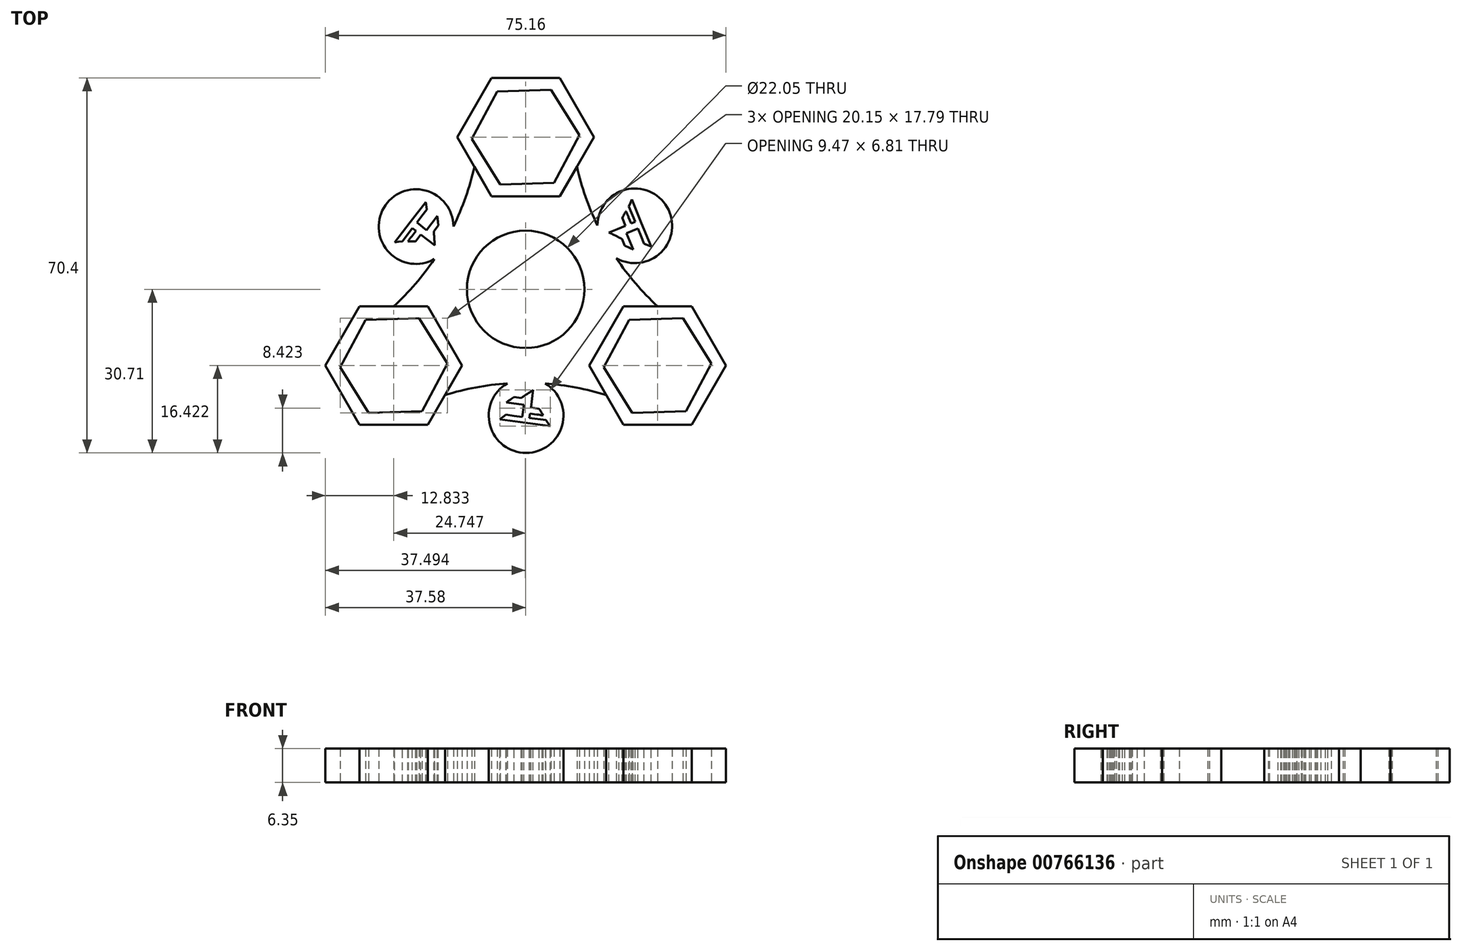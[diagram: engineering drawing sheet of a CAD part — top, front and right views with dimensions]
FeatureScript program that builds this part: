
annotation { "Feature Type Name" : "Feature", "Feature Type Description" : "" }
export const myFeature = defineFeature(function(context is Context, id is Id, definition is map)
    precondition{}
    {
        {
            var Q0;
            Q0=qCreatedBy(makeId("Top.planeOp"),FACE);
            var sketch = newSketch(context, id + "F0", { "sketchPlane" : qUnion([Q0])});
            skCircle(sketch, "E0.cCircle", {"center": v(0, 28.57) * mm, "radius": 8.73 * mm, "construction": true});
            skLineSegment(sketch, "E0.0", {"start": v(-4.75, 19.68) * mm, "end": v(-10.08, 28.24) * mm});
            skLineSegment(sketch, "E0.1", {"start": v(-10.08, 28.24) * mm, "end": v(-5.33, 37.14) * mm});
            skLineSegment(sketch, "E0.2", {"start": v(-5.33, 37.14) * mm, "end": v(4.75, 37.47) * mm});
            skLineSegment(sketch, "E0.3", {"start": v(4.75, 37.47) * mm, "end": v(10.08, 28.9) * mm});
            skLineSegment(sketch, "E0.4", {"start": v(10.08, 28.9) * mm, "end": v(5.33, 20.01) * mm});
            skLineSegment(sketch, "E0.5", {"start": v(5.33, 20.01) * mm, "end": v(-4.75, 19.68) * mm});
            skPoint(sketch, "E0.0.midPoint", {"position": v(-7.41, 23.96) * mm});
            skCircle(sketch, "E1.cCircle", {"center": v(0, 28.57) * mm, "radius": 11.11 * mm, "construction": true});
            skLineSegment(sketch, "E1.0", {"start": v(6.42, 17.46) * mm, "end": v(-6.42, 17.46) * mm});
            skLineSegment(sketch, "E1.1", {"start": v(-6.42, 17.46) * mm, "end": v(-12.83, 28.57) * mm});
            skLineSegment(sketch, "E1.2", {"start": v(-12.83, 28.57) * mm, "end": v(-6.42, 39.69) * mm});
            skLineSegment(sketch, "E1.3", {"start": v(-6.42, 39.69) * mm, "end": v(6.42, 39.69) * mm});
            skLineSegment(sketch, "E1.4", {"start": v(6.42, 39.69) * mm, "end": v(12.83, 28.57) * mm});
            skLineSegment(sketch, "E1.5", {"start": v(12.83, 28.57) * mm, "end": v(6.42, 17.46) * mm});
            skPoint(sketch, "E1.0.midPoint", {"position": v(0, 17.46) * mm});
            skLineSegment(sketch, "E2.1.0", {"start": v(-30.07, -5.73) * mm, "end": v(-20, -5.4) * mm});
            skPoint(sketch, "E2.1.1", {"position": v(-17.05, -18.4) * mm});
            skPoint(sketch, "E2.1.2", {"position": v(-15.12, -8.73) * mm});
            skLineSegment(sketch, "E2.1.3", {"start": v(-31.16, -3.17) * mm, "end": v(-18.33, -3.17) * mm});
            skLineSegment(sketch, "E2.1.4", {"start": v(-11.92, -14.29) * mm, "end": v(-18.33, -25.4) * mm});
            skLineSegment(sketch, "E2.1.5", {"start": v(-18.33, -3.17) * mm, "end": v(-11.92, -14.29) * mm});
            skLineSegment(sketch, "E2.1.6", {"start": v(-20, -5.4) * mm, "end": v(-14.67, -13.95) * mm});
            skLineSegment(sketch, "E2.1.7", {"start": v(-14.67, -13.95) * mm, "end": v(-19.42, -22.85) * mm});
            skLineSegment(sketch, "E2.1.8", {"start": v(-18.33, -25.4) * mm, "end": v(-31.16, -25.4) * mm});
            skCircle(sketch, "E2.1.9", {"center": v(-24.75, -14.29) * mm, "radius": 11.11 * mm, "construction": true});
            skLineSegment(sketch, "E2.1.10", {"start": v(-31.16, -25.4) * mm, "end": v(-37.58, -14.29) * mm});
            skCircle(sketch, "E2.1.11", {"center": v(-24.75, -14.29) * mm, "radius": 8.73 * mm, "construction": true});
            skLineSegment(sketch, "E2.1.12", {"start": v(-19.42, -22.85) * mm, "end": v(-29.5, -23.18) * mm});
            skLineSegment(sketch, "E2.1.13", {"start": v(-34.82, -14.62) * mm, "end": v(-30.07, -5.73) * mm});
            skLineSegment(sketch, "E2.1.14", {"start": v(-37.58, -14.29) * mm, "end": v(-31.16, -3.17) * mm});
            skLineSegment(sketch, "E2.1.15", {"start": v(-29.5, -23.18) * mm, "end": v(-34.82, -14.62) * mm});
            skLineSegment(sketch, "E2.2.0", {"start": v(20, -23.18) * mm, "end": v(14.67, -14.62) * mm});
            skPoint(sketch, "E2.2.1", {"position": v(24.46, -5.56) * mm});
            skPoint(sketch, "E2.2.2", {"position": v(15.12, -8.73) * mm});
            skLineSegment(sketch, "E2.2.3", {"start": v(18.33, -25.4) * mm, "end": v(11.92, -14.29) * mm});
            skLineSegment(sketch, "E2.2.4", {"start": v(18.33, -3.18) * mm, "end": v(31.16, -3.18) * mm});
            skLineSegment(sketch, "E2.2.5", {"start": v(11.92, -14.29) * mm, "end": v(18.33, -3.18) * mm});
            skLineSegment(sketch, "E2.2.6", {"start": v(14.67, -14.62) * mm, "end": v(19.42, -5.73) * mm});
            skLineSegment(sketch, "E2.2.7", {"start": v(19.42, -5.73) * mm, "end": v(29.5, -5.4) * mm});
            skLineSegment(sketch, "E2.2.8", {"start": v(31.16, -3.18) * mm, "end": v(37.58, -14.29) * mm});
            skCircle(sketch, "E2.2.9", {"center": v(24.75, -14.29) * mm, "radius": 11.11 * mm, "construction": true});
            skLineSegment(sketch, "E2.2.10", {"start": v(37.58, -14.29) * mm, "end": v(31.16, -25.4) * mm});
            skCircle(sketch, "E2.2.11", {"center": v(24.75, -14.29) * mm, "radius": 8.73 * mm, "construction": true});
            skLineSegment(sketch, "E2.2.12", {"start": v(29.5, -5.4) * mm, "end": v(34.82, -13.95) * mm});
            skLineSegment(sketch, "E2.2.13", {"start": v(30.07, -22.85) * mm, "end": v(20, -23.18) * mm});
            skLineSegment(sketch, "E2.2.14", {"start": v(31.16, -25.4) * mm, "end": v(18.33, -25.4) * mm});
            skLineSegment(sketch, "E2.2.15", {"start": v(34.82, -13.95) * mm, "end": v(30.07, -22.85) * mm});
            skPoint(sketch, "E2.center", {"position": v(0, 0) * mm});
            skSolve(sketch);
        }
        {
            var Q0;
            Q0=qCreatedBy(makeId("Top.planeOp"),FACE);
            var sketch = newSketch(context, id + "F1", { "sketchPlane" : qUnion([Q0])});
            skLineSegment(sketch, "E3.0", {"start": v(6.42, 39.69) * mm, "end": v(12.83, 28.57) * mm});
            skLineSegment(sketch, "E3.1", {"start": v(-29.5, -23.18) * mm, "end": v(-34.82, -14.62) * mm});
            skLineSegment(sketch, "E3.2", {"start": v(-34.82, -14.62) * mm, "end": v(-30.07, -5.73) * mm});
            skLineSegment(sketch, "E3.3", {"start": v(34.82, -13.95) * mm, "end": v(30.07, -22.85) * mm});
            skCircle(sketch, "E3.4", {"center": v(-24.75, -14.29) * mm, "radius": 8.73 * mm});
            skLineSegment(sketch, "E3.5", {"start": v(30.07, -22.85) * mm, "end": v(20, -23.18) * mm});
            skLineSegment(sketch, "E3.6", {"start": v(29.5, -5.4) * mm, "end": v(34.82, -13.95) * mm});
            skLineSegment(sketch, "E3.7", {"start": v(-31.16, -25.4) * mm, "end": v(-37.58, -14.29) * mm});
            skLineSegment(sketch, "E3.8", {"start": v(11.92, -14.29) * mm, "end": v(18.33, -3.18) * mm});
            skLineSegment(sketch, "E3.9", {"start": v(18.33, -25.4) * mm, "end": v(11.92, -14.29) * mm});
            skLineSegment(sketch, "E3.10", {"start": v(37.58, -14.29) * mm, "end": v(31.16, -25.4) * mm});
            skLineSegment(sketch, "E3.11", {"start": v(-18.33, -25.4) * mm, "end": v(-31.16, -25.4) * mm});
            skLineSegment(sketch, "E3.12", {"start": v(31.16, -3.18) * mm, "end": v(37.58, -14.29) * mm});
            skLineSegment(sketch, "E3.13", {"start": v(-20, -5.4) * mm, "end": v(-14.67, -13.95) * mm});
            skLineSegment(sketch, "E3.14", {"start": v(14.67, -14.62) * mm, "end": v(19.42, -5.73) * mm});
            skLineSegment(sketch, "E3.15", {"start": v(-11.92, -14.29) * mm, "end": v(-18.33, -25.4) * mm});
            skCircle(sketch, "E3.16", {"center": v(0, 0) * mm, "radius": 11.02 * mm});
            skCircle(sketch, "E3.17", {"center": v(0, 0) * mm, "radius": 14.29 * mm});
            skLineSegment(sketch, "E3.18", {"start": v(12.83, 28.57) * mm, "end": v(6.42, 17.46) * mm});
            skLineSegment(sketch, "E3.19", {"start": v(-30.07, -5.73) * mm, "end": v(-20, -5.4) * mm});
            skLineSegment(sketch, "E3.20", {"start": v(-31.16, -3.17) * mm, "end": v(-18.33, -3.17) * mm});
            skLineSegment(sketch, "E3.21", {"start": v(20, -23.18) * mm, "end": v(14.67, -14.62) * mm});
            skCircle(sketch, "E3.22", {"center": v(0, 28.57) * mm, "radius": 8.73 * mm});
            skLineSegment(sketch, "E3.23", {"start": v(-10.08, 28.24) * mm, "end": v(-5.33, 37.14) * mm});
            skLineSegment(sketch, "E3.24", {"start": v(-5.33, 37.14) * mm, "end": v(4.75, 37.47) * mm});
            skLineSegment(sketch, "E3.25", {"start": v(-19.42, -22.85) * mm, "end": v(-29.5, -23.18) * mm});
            skLineSegment(sketch, "E3.26", {"start": v(10.08, 28.9) * mm, "end": v(5.33, 20.01) * mm});
            skLineSegment(sketch, "E3.27", {"start": v(4.75, 37.47) * mm, "end": v(10.08, 28.9) * mm});
            skLineSegment(sketch, "E3.28", {"start": v(31.16, -25.4) * mm, "end": v(18.33, -25.4) * mm});
            skCircle(sketch, "E3.29", {"center": v(0, 28.57) * mm, "radius": 11.11 * mm});
            skCircle(sketch, "E3.30", {"center": v(24.75, -14.29) * mm, "radius": 8.73 * mm});
            skLineSegment(sketch, "E3.31", {"start": v(18.33, -3.18) * mm, "end": v(31.16, -3.18) * mm});
            skCircle(sketch, "E3.32", {"center": v(-24.75, -14.29) * mm, "radius": 11.11 * mm});
            skLineSegment(sketch, "E3.33", {"start": v(6.42, 17.46) * mm, "end": v(-6.42, 17.46) * mm});
            skLineSegment(sketch, "E3.34", {"start": v(-6.42, 17.46) * mm, "end": v(-12.83, 28.57) * mm});
            skLineSegment(sketch, "E3.35", {"start": v(-37.58, -14.29) * mm, "end": v(-31.16, -3.17) * mm});
            skCircle(sketch, "E3.36", {"center": v(24.75, -14.29) * mm, "radius": 11.11 * mm});
            skLineSegment(sketch, "E3.37", {"start": v(-12.83, 28.57) * mm, "end": v(-6.42, 39.69) * mm});
            skLineSegment(sketch, "E3.38", {"start": v(-6.42, 39.69) * mm, "end": v(6.42, 39.69) * mm});
            skLineSegment(sketch, "E3.39", {"start": v(-18.33, -3.17) * mm, "end": v(-11.92, -14.29) * mm});
            skPoint(sketch, "E4.endSnap0", {"position": v(-25.03, -5.56) * mm});
            skArc(sketch, "E5", {"start": v(9.62, 23.02) * mm, "mid": v(15.2, 8.77) * mm, "end": v(24.75, -3.18) * mm});
            skArc(sketch, "E6", {"start": v(-24.75, -3.18) * mm, "mid": v(-15.2, 8.77) * mm, "end": v(-9.62, 23.02) * mm});
            skArc(sketch, "E7", {"start": v(15.12, -19.84) * mm, "mid": v(0, -17.54) * mm, "end": v(-15.12, -19.84) * mm});
            skCircle(sketch, "E8", {"center": v(-20.57, 11.77) * mm, "radius": 7 * mm});
            skCircle(sketch, "E9.1.0", {"center": v(0.09, -23.7) * mm, "radius": 7 * mm});
            skCircle(sketch, "E9.2.0", {"center": v(20.48, 11.93) * mm, "radius": 7 * mm});
            skSolve(sketch);
        }
        {
            var Q0;
            {var subQ0=sQuery(id+"F1.wireOp",EDGE,"E8");var subQ1=sQuery(id+"F1.wireOp",EDGE,"E6");var subQ2=makeQuery(id+"F1.imprint","INTERSECT",VERTEX,{"disambiguationData":[OD(0.0)],"derivedFrom":[subQ1,subQ0]});Q0=makeQuery(id+"F1.imprint","IMPRINT",FACE,{"disambiguationData":[TD([[makeQuery(id+"F1.imprint","IMPRINT",EDGE,{"disambiguationData":[TD([[subQ2,-1.0]])],"derivedFrom":subQ1}),1.0]])]});}
            var Q1;
            {var subQ0=sQuery(id+"F1.wireOp",EDGE,"E9.2.0");var subQ1=sQuery(id+"F1.wireOp",EDGE,"E5");var subQ2=makeQuery(id+"F1.imprint","INTERSECT",VERTEX,{"disambiguationData":[OD(0.0)],"derivedFrom":[subQ1,subQ0]});Q1=makeQuery(id+"F1.imprint","IMPRINT",FACE,{"disambiguationData":[TD([[makeQuery(id+"F1.imprint","IMPRINT",EDGE,{"disambiguationData":[TD([[subQ2,-1.0]])],"derivedFrom":subQ1}),1.0]])]});}
            var Q2;
            Q2=makeQuery(id+"F0.imprint","IMPRINT",FACE,{"disambiguationData":[TD([[makeQuery(id+"F0.imprint","IMPRINT",EDGE,{"derivedFrom":sQuery(id+"F0.wireOp",EDGE,"E2.2.0")}),1.0]])]});
            var Q3;
            Q3=makeQuery(id+"F0.imprint","IMPRINT",FACE,{"disambiguationData":[TD([[makeQuery(id+"F0.imprint","IMPRINT",EDGE,{"derivedFrom":sQuery(id+"F0.wireOp",EDGE,"E2.1.0")}),1.0]])]});
            var Q4;
            {var subQ0=sQuery(id+"F1.wireOp",EDGE,"E9.1.0");var subQ1=sQuery(id+"F1.wireOp",EDGE,"E7");var subQ2=makeQuery(id+"F1.imprint","INTERSECT",VERTEX,{"disambiguationData":[OD(0.0)],"derivedFrom":[subQ1,subQ0]});Q4=makeQuery(id+"F1.imprint","IMPRINT",FACE,{"disambiguationData":[TD([[makeQuery(id+"F1.imprint","IMPRINT",EDGE,{"disambiguationData":[TD([[subQ2,-1.0]])],"derivedFrom":subQ1}),1.0]])]});}
            var Q5;
            Q5=makeQuery(id+"F1.imprint","IMPRINT",FACE,{"disambiguationData":[TD([[makeQuery(id+"F1.imprint","IMPRINT",EDGE,{"derivedFrom":sQuery(id+"F1.wireOp",EDGE,"E3.17")}),-1.0]])]});
            var Q6;
            {var subQ0=sQuery(id+"F1.wireOp",EDGE,"E9.2.0");var subQ1=sQuery(id+"F1.wireOp",EDGE,"E5");var subQ2=makeQuery(id+"F1.imprint","INTERSECT",VERTEX,{"disambiguationData":[OD(0.0)],"derivedFrom":[subQ1,subQ0]});Q6=makeQuery(id+"F1.imprint","IMPRINT",FACE,{"disambiguationData":[TD([[makeQuery(id+"F1.imprint","IMPRINT",EDGE,{"disambiguationData":[TD([[subQ2,-1.0]])],"derivedFrom":subQ1}),-1.0]])]});}
            var Q7;
            Q7=makeQuery(id+"F1.imprint","IMPRINT",FACE,{"disambiguationData":[TD([[makeQuery(id+"F1.imprint","IMPRINT",EDGE,{"derivedFrom":sQuery(id+"F1.wireOp",EDGE,"E3.16")}),-1.0]])]});
            var Q8;
            {var subQ0=sQuery(id+"F1.wireOp",EDGE,"E8");var subQ1=sQuery(id+"F1.wireOp",EDGE,"E6");var subQ2=makeQuery(id+"F1.imprint","INTERSECT",VERTEX,{"disambiguationData":[OD(0.0)],"derivedFrom":[subQ1,subQ0]});Q8=makeQuery(id+"F1.imprint","IMPRINT",FACE,{"disambiguationData":[TD([[makeQuery(id+"F1.imprint","IMPRINT",EDGE,{"disambiguationData":[TD([[subQ2,-1.0]])],"derivedFrom":subQ1}),-1.0]])]});}
            var Q9;
            {var subQ0=sQuery(id+"F1.wireOp",EDGE,"E9.1.0");var subQ1=sQuery(id+"F1.wireOp",EDGE,"E7");var subQ2=makeQuery(id+"F1.imprint","INTERSECT",VERTEX,{"disambiguationData":[OD(0.0)],"derivedFrom":[subQ1,subQ0]});Q9=makeQuery(id+"F1.imprint","IMPRINT",FACE,{"disambiguationData":[TD([[makeQuery(id+"F1.imprint","IMPRINT",EDGE,{"disambiguationData":[TD([[subQ2,-1.0]])],"derivedFrom":subQ1}),-1.0]])]});}
            var Q10;
            Q10=makeQuery(id+"F0.imprint","IMPRINT",FACE,{"disambiguationData":[TD([[makeQuery(id+"F0.imprint","IMPRINT",EDGE,{"derivedFrom":sQuery(id+"F0.wireOp",EDGE,"E0.0")}),1.0]])]});
            extrude(context, id + "F2", {"entities" : qUnion([Q0, Q1, Q2, Q3, Q4, Q5, Q6, Q7, Q8, Q9, Q10]), "depth" : 6.35 * mm, "offsetDistance" : 25.4 * mm});
        }
        {
            var Q0;
            Q0=makeQuery(id+"F2.opExtrude","CAP_FACE",FACE,{"disambiguationData":[OSD([sQuery(id+"F1.wireOp",EDGE,"E3.8"),sQuery(id+"F1.wireOp",EDGE,"E3.9"),sQuery(id+"F1.wireOp",EDGE,"E3.15"),sQuery(id+"F1.wireOp",EDGE,"E3.16"),sQuery(id+"F1.wireOp",EDGE,"E3.18"),sQuery(id+"F1.wireOp",EDGE,"E3.20"),sQuery(id+"F1.wireOp",EDGE,"E3.31"),sQuery(id+"F1.wireOp",EDGE,"E3.33"),sQuery(id+"F1.wireOp",EDGE,"E3.34"),sQuery(id+"F1.wireOp",EDGE,"E3.39"),sQuery(id+"F1.wireOp",EDGE,"E5"),sQuery(id+"F1.wireOp",EDGE,"E6"),sQuery(id+"F1.wireOp",EDGE,"E7"),sQuery(id+"F1.wireOp",EDGE,"E8"),sQuery(id+"F1.wireOp",EDGE,"E9.1.0"),sQuery(id+"F1.wireOp",EDGE,"E9.2.0")])],"isStart":false});
            var sketch = newSketch(context, id + "F3", { "sketchPlane" : qUnion([Q0])});
            skLineSegment(sketch, "E10", {"start": v(-23.87, 8.91) * mm, "end": v(-23.15, 9) * mm});
            skLineSegment(sketch, "E11", {"start": v(-23.15, 9) * mm, "end": v(-21.26, 11.45) * mm});
            skLineSegment(sketch, "E12", {"start": v(-21.26, 11.45) * mm, "end": v(-20.6, 10.94) * mm});
            skLineSegment(sketch, "E13", {"start": v(-20.6, 10.94) * mm, "end": v(-21.37, 9.96) * mm});
            skLineSegment(sketch, "E14", {"start": v(-21.37, 9.96) * mm, "end": v(-21.43, 9.9) * mm});
            skLineSegment(sketch, "E15", {"start": v(-21.43, 9.9) * mm, "end": v(-21.6, 9.67) * mm});
            skLineSegment(sketch, "E16", {"start": v(-21.6, 9.67) * mm, "end": v(-21.78, 9.44) * mm});
            skLineSegment(sketch, "E17", {"start": v(-21.78, 9.44) * mm, "end": v(-21.91, 9.27) * mm});
            skLineSegment(sketch, "E18", {"start": v(-21.91, 9.27) * mm, "end": v(-22, 9.15) * mm});
            skLineSegment(sketch, "E19", {"start": v(-22, 9.15) * mm, "end": v(-22.07, 9.06) * mm});
            skLineSegment(sketch, "E20", {"start": v(-22.07, 9.06) * mm, "end": v(-22.1, 9.01) * mm});
            skLineSegment(sketch, "E21", {"start": v(-22.1, 9.01) * mm, "end": v(-22.11, 8.99) * mm});
            skLineSegment(sketch, "E22", {"start": v(-22.11, 8.99) * mm, "end": v(-22.11, 8.98) * mm});
            skLineSegment(sketch, "E23", {"start": v(-22.11, 8.98) * mm, "end": v(-22.1, 8.98) * mm});
            skLineSegment(sketch, "E24", {"start": v(-22.1, 8.98) * mm, "end": v(-22.1, 8.98) * mm});
            skLineSegment(sketch, "E25", {"start": v(-22.1, 8.98) * mm, "end": v(-22.07, 8.98) * mm});
            skLineSegment(sketch, "E26", {"start": v(-22.07, 8.98) * mm, "end": v(-21.97, 8.98) * mm});
            skLineSegment(sketch, "E27", {"start": v(-21.97, 8.98) * mm, "end": v(-21.82, 8.98) * mm});
            skLineSegment(sketch, "E28", {"start": v(-21.82, 8.98) * mm, "end": v(-21.64, 8.98) * mm});
            skLineSegment(sketch, "E29", {"start": v(-21.64, 8.98) * mm, "end": v(-21.43, 8.99) * mm});
            skLineSegment(sketch, "E30", {"start": v(-21.43, 8.99) * mm, "end": v(-21.2, 9) * mm});
            skLineSegment(sketch, "E31", {"start": v(-21.2, 9) * mm, "end": v(-20.98, 9) * mm});
            skLineSegment(sketch, "E32", {"start": v(-20.98, 9) * mm, "end": v(-20.82, 9) * mm});
            skLineSegment(sketch, "E33", {"start": v(-20.82, 9) * mm, "end": v(-20.76, 9) * mm});
            skLineSegment(sketch, "E34", {"start": v(-20.76, 9) * mm, "end": v(-20.67, 9) * mm});
            skLineSegment(sketch, "E35", {"start": v(-20.67, 9) * mm, "end": v(-19.7, 10.25) * mm});
            skLineSegment(sketch, "E36", {"start": v(-19.7, 10.25) * mm, "end": v(-18.38, 9.23) * mm});
            skLineSegment(sketch, "E37", {"start": v(-18.38, 9.23) * mm, "end": v(-17.06, 8.21) * mm});
            skLineSegment(sketch, "E38", {"start": v(-17.06, 8.21) * mm, "end": v(-17.07, 8.4) * mm});
            skLineSegment(sketch, "E39", {"start": v(-17.07, 8.4) * mm, "end": v(-17.07, 8.42) * mm});
            skLineSegment(sketch, "E40", {"start": v(-17.07, 8.42) * mm, "end": v(-17.08, 8.51) * mm});
            skLineSegment(sketch, "E41", {"start": v(-17.08, 8.51) * mm, "end": v(-17.1, 8.71) * mm});
            skLineSegment(sketch, "E42", {"start": v(-17.1, 8.71) * mm, "end": v(-17.11, 8.97) * mm});
            skLineSegment(sketch, "E43", {"start": v(-17.11, 8.97) * mm, "end": v(-17.13, 9.26) * mm});
            skLineSegment(sketch, "E44", {"start": v(-17.13, 9.26) * mm, "end": v(-17.15, 9.56) * mm});
            skLineSegment(sketch, "E45", {"start": v(-17.15, 9.56) * mm, "end": v(-17.17, 9.84) * mm});
            skLineSegment(sketch, "E46", {"start": v(-17.17, 9.84) * mm, "end": v(-17.18, 10.09) * mm});
            skLineSegment(sketch, "E47", {"start": v(-17.18, 10.09) * mm, "end": v(-17.19, 10.22) * mm});
            skLineSegment(sketch, "E48", {"start": v(-17.19, 10.22) * mm, "end": v(-17.2, 10.27) * mm});
            skLineSegment(sketch, "E49", {"start": v(-17.2, 10.27) * mm, "end": v(-17.2, 10.3) * mm});
            skLineSegment(sketch, "E50", {"start": v(-17.2, 10.3) * mm, "end": v(-17.2, 10.37) * mm});
            skLineSegment(sketch, "E51", {"start": v(-17.2, 10.37) * mm, "end": v(-17.2, 10.5) * mm});
            skLineSegment(sketch, "E52", {"start": v(-17.2, 10.5) * mm, "end": v(-17.22, 10.6) * mm});
            skLineSegment(sketch, "E53", {"start": v(-17.22, 10.6) * mm, "end": v(-17.22, 10.68) * mm});
            skLineSegment(sketch, "E54", {"start": v(-17.22, 10.68) * mm, "end": v(-17.22, 10.7) * mm});
            skLineSegment(sketch, "E55", {"start": v(-17.22, 10.7) * mm, "end": v(-17.24, 10.91) * mm});
            skLineSegment(sketch, "E56", {"start": v(-17.24, 10.91) * mm, "end": v(-16.4, 12) * mm});
            skLineSegment(sketch, "E57", {"start": v(-16.4, 12) * mm, "end": v(-16.47, 12.7) * mm});
            skLineSegment(sketch, "E58", {"start": v(-16.47, 12.7) * mm, "end": v(-16.47, 12.73) * mm});
            skLineSegment(sketch, "E59", {"start": v(-16.47, 12.73) * mm, "end": v(-16.48, 12.83) * mm});
            skLineSegment(sketch, "E60", {"start": v(-16.48, 12.83) * mm, "end": v(-16.5, 12.97) * mm});
            skLineSegment(sketch, "E61", {"start": v(-16.5, 12.97) * mm, "end": v(-16.51, 13.1) * mm});
            skLineSegment(sketch, "E62", {"start": v(-16.51, 13.1) * mm, "end": v(-16.52, 13.23) * mm});
            skLineSegment(sketch, "E63", {"start": v(-16.52, 13.23) * mm, "end": v(-16.54, 13.34) * mm});
            skLineSegment(sketch, "E64", {"start": v(-16.54, 13.34) * mm, "end": v(-16.55, 13.44) * mm});
            skLineSegment(sketch, "E65", {"start": v(-16.55, 13.44) * mm, "end": v(-16.56, 13.51) * mm});
            skLineSegment(sketch, "E66", {"start": v(-16.56, 13.51) * mm, "end": v(-16.56, 13.55) * mm});
            skLineSegment(sketch, "E67", {"start": v(-16.56, 13.55) * mm, "end": v(-16.56, 13.56) * mm});
            skLineSegment(sketch, "E68", {"start": v(-16.56, 13.56) * mm, "end": v(-16.58, 13.74) * mm});
            skLineSegment(sketch, "E69", {"start": v(-16.58, 13.74) * mm, "end": v(-18.6, 11.12) * mm});
            skLineSegment(sketch, "E70", {"start": v(-18.6, 11.12) * mm, "end": v(-20.42, 12.53) * mm});
            skLineSegment(sketch, "E71", {"start": v(-20.42, 12.53) * mm, "end": v(-19.48, 13.74) * mm});
            skLineSegment(sketch, "E72", {"start": v(-19.48, 13.74) * mm, "end": v(-18.55, 14.96) * mm});
            skLineSegment(sketch, "E73", {"start": v(-18.55, 14.96) * mm, "end": v(-18.73, 16.38) * mm});
            skLineSegment(sketch, "E74", {"start": v(-18.73, 16.38) * mm, "end": v(-21.65, 12.6) * mm});
            skLineSegment(sketch, "E75", {"start": v(-21.65, 12.6) * mm, "end": v(-24.57, 8.82) * mm});
            skLineSegment(sketch, "E76", {"start": v(-24.57, 8.82) * mm, "end": v(-23.87, 8.91) * mm});
            skLineSegment(sketch, "E77.2.1", {"start": v(-3396.23, 1573.93) * mm, "end": v(-3401, 1573.93) * mm});
            skPoint(sketch, "E77.center", {"position": v(0, 0) * mm});
            skLineSegment(sketch, "E78.1.0", {"start": v(-4.82, -24.4) * mm, "end": v(-0.09, -25.05) * mm});
            skLineSegment(sketch, "E78.1.1", {"start": v(-3.6, -21.23) * mm, "end": v(-0.33, -21.68) * mm});
            skLineSegment(sketch, "E78.1.2", {"start": v(-0.09, -25.05) * mm, "end": v(4.65, -25.7) * mm});
            skLineSegment(sketch, "E78.1.3", {"start": v(2.54, -22.4) * mm, "end": v(0.98, -22.2) * mm});
            skLineSegment(sketch, "E78.1.4", {"start": v(3.78, -24.56) * mm, "end": v(0.71, -24.14) * mm});
            skLineSegment(sketch, "E78.1.5", {"start": v(0.71, -24.14) * mm, "end": v(0.82, -23.3) * mm});
            skLineSegment(sketch, "E78.1.6", {"start": v(-0.33, -21.68) * mm, "end": v(-0.64, -23.94) * mm});
            skLineSegment(sketch, "E78.1.7", {"start": v(-0.64, -23.94) * mm, "end": v(-2.16, -23.74) * mm});
            skLineSegment(sketch, "E78.1.8", {"start": v(1.2, -20.54) * mm, "end": v(1.42, -18.88) * mm});
            skLineSegment(sketch, "E78.1.9", {"start": v(-2.16, -23.74) * mm, "end": v(-3.68, -23.54) * mm});
            skLineSegment(sketch, "E78.1.10", {"start": v(0.98, -22.2) * mm, "end": v(1.2, -20.54) * mm});
            skLineSegment(sketch, "E78.1.11", {"start": v(-3.68, -23.54) * mm, "end": v(-4.82, -24.4) * mm});
            skLineSegment(sketch, "E78.1.12", {"start": v(4.21, -25.13) * mm, "end": v(3.78, -24.56) * mm});
            skLineSegment(sketch, "E78.1.13", {"start": v(4.65, -25.7) * mm, "end": v(4.21, -25.13) * mm});
            skLineSegment(sketch, "E78.1.14", {"start": v(0.82, -23.3) * mm, "end": v(2.06, -23.49) * mm});
            skLineSegment(sketch, "E78.1.15", {"start": v(-0.83, -20.39) * mm, "end": v(-2.2, -20.2) * mm});
            skLineSegment(sketch, "E78.1.16", {"start": v(-2.2, -20.2) * mm, "end": v(-2.76, -20.6) * mm});
            skLineSegment(sketch, "E78.1.17", {"start": v(2.7, -22.67) * mm, "end": v(2.61, -22.53) * mm});
            skLineSegment(sketch, "E78.1.18", {"start": v(1.24, -19) * mm, "end": v(1.17, -19.05) * mm});
            skLineSegment(sketch, "E78.1.19", {"start": v(2.82, -22.86) * mm, "end": v(2.7, -22.67) * mm});
            skLineSegment(sketch, "E78.1.20", {"start": v(1.27, -18.98) * mm, "end": v(1.24, -19) * mm});
            skLineSegment(sketch, "E78.1.21", {"start": v(1.42, -18.88) * mm, "end": v(1.27, -18.98) * mm});
            skLineSegment(sketch, "E78.1.22", {"start": v(2.59, -22.48) * mm, "end": v(2.54, -22.4) * mm});
            skLineSegment(sketch, "E78.1.23", {"start": v(-3.46, -21.12) * mm, "end": v(-3.6, -21.23) * mm});
            skLineSegment(sketch, "E78.1.24", {"start": v(-0.66, -20.27) * mm, "end": v(-0.83, -20.39) * mm});
            skLineSegment(sketch, "E78.1.25", {"start": v(2.61, -22.53) * mm, "end": v(2.59, -22.48) * mm});
            skLineSegment(sketch, "E78.1.26", {"start": v(1.17, -19.05) * mm, "end": v(1, -19.16) * mm});
            skLineSegment(sketch, "E78.1.27", {"start": v(-2.79, -20.63) * mm, "end": v(-2.87, -20.7) * mm});
            skLineSegment(sketch, "E78.1.28", {"start": v(-3.2, -20.93) * mm, "end": v(-3.29, -21) * mm});
            skLineSegment(sketch, "E78.1.29", {"start": v(-2.87, -20.7) * mm, "end": v(-2.99, -20.77) * mm});
            skLineSegment(sketch, "E78.1.30", {"start": v(-3.1, -20.85) * mm, "end": v(-3.2, -20.93) * mm});
            skLineSegment(sketch, "E78.1.31", {"start": v(-3.42, -21.1) * mm, "end": v(-3.45, -21.12) * mm});
            skLineSegment(sketch, "E78.1.32", {"start": v(-0.64, -20.25) * mm, "end": v(-0.66, -20.27) * mm});
            skLineSegment(sketch, "E78.1.33", {"start": v(-2.99, -20.77) * mm, "end": v(-3.1, -20.85) * mm});
            skLineSegment(sketch, "E78.1.34", {"start": v(-2.76, -20.6) * mm, "end": v(-2.79, -20.63) * mm});
            skLineSegment(sketch, "E78.1.35", {"start": v(-3.45, -21.12) * mm, "end": v(-3.46, -21.12) * mm});
            skLineSegment(sketch, "E78.1.36", {"start": v(0.79, -19.3) * mm, "end": v(0.55, -19.46) * mm});
            skLineSegment(sketch, "E78.1.37", {"start": v(0.3, -19.63) * mm, "end": v(0.06, -19.79) * mm});
            skLineSegment(sketch, "E78.1.38", {"start": v(-0.14, -19.92) * mm, "end": v(-0.26, -20) * mm});
            skLineSegment(sketch, "E78.1.39", {"start": v(-0.58, -20.21) * mm, "end": v(-0.64, -20.25) * mm});
            skLineSegment(sketch, "E78.1.40", {"start": v(1, -19.16) * mm, "end": v(0.79, -19.3) * mm});
            skLineSegment(sketch, "E78.1.41", {"start": v(0.55, -19.46) * mm, "end": v(0.3, -19.63) * mm});
            skLineSegment(sketch, "E78.1.42", {"start": v(0.06, -19.79) * mm, "end": v(-0.14, -19.92) * mm});
            skLineSegment(sketch, "E78.1.43", {"start": v(-3.36, -21.05) * mm, "end": v(-3.42, -21.1) * mm});
            skLineSegment(sketch, "E78.1.44", {"start": v(-0.48, -20.15) * mm, "end": v(-0.58, -20.21) * mm});
            skLineSegment(sketch, "E78.1.45", {"start": v(-0.38, -20.08) * mm, "end": v(-0.48, -20.15) * mm});
            skLineSegment(sketch, "E78.1.46", {"start": v(-3.29, -21) * mm, "end": v(-3.36, -21.05) * mm});
            skLineSegment(sketch, "E78.1.47", {"start": v(-0.32, -20.04) * mm, "end": v(-0.38, -20.08) * mm});
            skLineSegment(sketch, "E78.1.48", {"start": v(-0.3, -20.02) * mm, "end": v(-0.32, -20.04) * mm});
            skLineSegment(sketch, "E78.1.49", {"start": v(-0.26, -20) * mm, "end": v(-0.3, -20.02) * mm});
            skLineSegment(sketch, "E78.1.50", {"start": v(3.26, -23.6) * mm, "end": v(3.2, -23.51) * mm});
            skLineSegment(sketch, "E78.1.51", {"start": v(2.15, -23.5) * mm, "end": v(2.43, -23.54) * mm});
            skLineSegment(sketch, "E78.1.52", {"start": v(3.04, -23.23) * mm, "end": v(2.93, -23.05) * mm});
            skLineSegment(sketch, "E78.1.53", {"start": v(2.71, -23.58) * mm, "end": v(2.93, -23.61) * mm});
            skLineSegment(sketch, "E78.1.54", {"start": v(3.27, -23.64) * mm, "end": v(3.28, -23.64) * mm});
            skLineSegment(sketch, "E78.1.55", {"start": v(2.93, -23.05) * mm, "end": v(2.82, -22.86) * mm});
            skLineSegment(sketch, "E78.1.56", {"start": v(2.43, -23.54) * mm, "end": v(2.71, -23.58) * mm});
            skLineSegment(sketch, "E78.1.57", {"start": v(3.13, -23.39) * mm, "end": v(3.04, -23.23) * mm});
            skLineSegment(sketch, "E78.1.58", {"start": v(3.24, -23.65) * mm, "end": v(3.27, -23.64) * mm});
            skLineSegment(sketch, "E78.1.59", {"start": v(2.06, -23.49) * mm, "end": v(2.15, -23.5) * mm});
            skLineSegment(sketch, "E78.1.60", {"start": v(3.19, -23.64) * mm, "end": v(3.24, -23.65) * mm});
            skLineSegment(sketch, "E78.1.61", {"start": v(3.08, -23.63) * mm, "end": v(3.19, -23.64) * mm});
            skLineSegment(sketch, "E78.1.62", {"start": v(2.93, -23.61) * mm, "end": v(3.08, -23.63) * mm});
            skLineSegment(sketch, "E78.1.63", {"start": v(3.28, -23.63) * mm, "end": v(3.26, -23.6) * mm});
            skLineSegment(sketch, "E78.1.64", {"start": v(3.28, -23.64) * mm, "end": v(3.28, -23.63) * mm});
            skLineSegment(sketch, "E78.1.65", {"start": v(3.28, -23.64) * mm, "end": v(3.28, -23.64) * mm});
            skLineSegment(sketch, "E78.1.66", {"start": v(3.2, -23.51) * mm, "end": v(3.13, -23.39) * mm});
            skLineSegment(sketch, "E78.2.0", {"start": v(23.55, 8.03) * mm, "end": v(21.74, 12.45) * mm});
            skLineSegment(sketch, "E78.2.1", {"start": v(20.2, 7.49) * mm, "end": v(18.94, 10.55) * mm});
            skLineSegment(sketch, "E78.2.2", {"start": v(21.74, 12.45) * mm, "end": v(19.93, 16.87) * mm});
            skLineSegment(sketch, "E78.2.3", {"start": v(18.13, 13.4) * mm, "end": v(18.73, 11.94) * mm});
            skLineSegment(sketch, "E78.2.4", {"start": v(19.38, 15.55) * mm, "end": v(20.55, 12.69) * mm});
            skLineSegment(sketch, "E78.2.5", {"start": v(20.55, 12.69) * mm, "end": v(19.77, 12.37) * mm});
            skLineSegment(sketch, "E78.2.6", {"start": v(18.94, 10.55) * mm, "end": v(21.06, 11.42) * mm});
            skLineSegment(sketch, "E78.2.7", {"start": v(21.06, 11.42) * mm, "end": v(21.64, 10) * mm});
            skLineSegment(sketch, "E78.2.8", {"start": v(17.18, 11.3) * mm, "end": v(15.64, 10.67) * mm});
            skLineSegment(sketch, "E78.2.9", {"start": v(21.64, 10) * mm, "end": v(22.23, 8.58) * mm});
            skLineSegment(sketch, "E78.2.10", {"start": v(18.73, 11.94) * mm, "end": v(17.18, 11.3) * mm});
            skLineSegment(sketch, "E78.2.11", {"start": v(22.23, 8.58) * mm, "end": v(23.55, 8.03) * mm});
            skLineSegment(sketch, "E78.2.12", {"start": v(19.65, 16.21) * mm, "end": v(19.38, 15.55) * mm});
            skLineSegment(sketch, "E78.2.13", {"start": v(19.93, 16.87) * mm, "end": v(19.65, 16.21) * mm});
            skLineSegment(sketch, "E78.2.14", {"start": v(19.77, 12.37) * mm, "end": v(19.31, 13.52) * mm});
            skLineSegment(sketch, "E78.2.15", {"start": v(18.07, 9.47) * mm, "end": v(18.6, 8.2) * mm});
            skLineSegment(sketch, "E78.2.16", {"start": v(18.6, 8.2) * mm, "end": v(19.22, 7.92) * mm});
            skLineSegment(sketch, "E78.2.17", {"start": v(18.28, 13.67) * mm, "end": v(18.2, 13.53) * mm});
            skLineSegment(sketch, "E78.2.18", {"start": v(15.83, 10.58) * mm, "end": v(15.91, 10.54) * mm});
            skLineSegment(sketch, "E78.2.19", {"start": v(18.39, 13.87) * mm, "end": v(18.28, 13.67) * mm});
            skLineSegment(sketch, "E78.2.20", {"start": v(15.8, 10.59) * mm, "end": v(15.83, 10.58) * mm});
            skLineSegment(sketch, "E78.2.21", {"start": v(15.64, 10.67) * mm, "end": v(15.8, 10.59) * mm});
            skLineSegment(sketch, "E78.2.22", {"start": v(18.18, 13.48) * mm, "end": v(18.13, 13.4) * mm});
            skLineSegment(sketch, "E78.2.23", {"start": v(20.02, 7.56) * mm, "end": v(20.2, 7.49) * mm});
            skLineSegment(sketch, "E78.2.24", {"start": v(17.88, 9.56) * mm, "end": v(18.07, 9.47) * mm});
            skLineSegment(sketch, "E78.2.25", {"start": v(18.2, 13.53) * mm, "end": v(18.18, 13.48) * mm});
            skLineSegment(sketch, "E78.2.26", {"start": v(15.91, 10.54) * mm, "end": v(16.1, 10.45) * mm});
            skLineSegment(sketch, "E78.2.27", {"start": v(19.26, 7.9) * mm, "end": v(19.36, 7.86) * mm});
            skLineSegment(sketch, "E78.2.28", {"start": v(19.72, 7.7) * mm, "end": v(19.82, 7.65) * mm});
            skLineSegment(sketch, "E78.2.29", {"start": v(19.36, 7.86) * mm, "end": v(19.48, 7.8) * mm});
            skLineSegment(sketch, "E78.2.30", {"start": v(19.6, 7.75) * mm, "end": v(19.72, 7.7) * mm});
            skLineSegment(sketch, "E78.2.31", {"start": v(19.98, 7.58) * mm, "end": v(20.01, 7.57) * mm});
            skLineSegment(sketch, "E78.2.32", {"start": v(17.86, 9.57) * mm, "end": v(17.88, 9.56) * mm});
            skLineSegment(sketch, "E78.2.33", {"start": v(19.48, 7.8) * mm, "end": v(19.6, 7.75) * mm});
            skLineSegment(sketch, "E78.2.34", {"start": v(19.22, 7.92) * mm, "end": v(19.26, 7.9) * mm});
            skLineSegment(sketch, "E78.2.35", {"start": v(20.01, 7.57) * mm, "end": v(20.02, 7.56) * mm});
            skLineSegment(sketch, "E78.2.36", {"start": v(16.32, 10.33) * mm, "end": v(16.58, 10.2) * mm});
            skLineSegment(sketch, "E78.2.37", {"start": v(16.85, 10.07) * mm, "end": v(17.1, 9.95) * mm});
            skLineSegment(sketch, "E78.2.38", {"start": v(17.33, 9.84) * mm, "end": v(17.45, 9.78) * mm});
            skLineSegment(sketch, "E78.2.39", {"start": v(17.8, 9.6) * mm, "end": v(17.86, 9.57) * mm});
            skLineSegment(sketch, "E78.2.40", {"start": v(16.1, 10.45) * mm, "end": v(16.32, 10.33) * mm});
            skLineSegment(sketch, "E78.2.41", {"start": v(16.58, 10.2) * mm, "end": v(16.85, 10.07) * mm});
            skLineSegment(sketch, "E78.2.42", {"start": v(17.1, 9.95) * mm, "end": v(17.33, 9.84) * mm});
            skLineSegment(sketch, "E78.2.43", {"start": v(19.9, 7.61) * mm, "end": v(19.98, 7.58) * mm});
            skLineSegment(sketch, "E78.2.44", {"start": v(17.7, 9.66) * mm, "end": v(17.8, 9.6) * mm});
            skLineSegment(sketch, "E78.2.45", {"start": v(17.58, 9.7) * mm, "end": v(17.7, 9.66) * mm});
            skLineSegment(sketch, "E78.2.46", {"start": v(19.82, 7.65) * mm, "end": v(19.9, 7.61) * mm});
            skLineSegment(sketch, "E78.2.47", {"start": v(17.51, 9.74) * mm, "end": v(17.58, 9.7) * mm});
            skLineSegment(sketch, "E78.2.48", {"start": v(17.49, 9.75) * mm, "end": v(17.51, 9.74) * mm});
            skLineSegment(sketch, "E78.2.49", {"start": v(17.45, 9.78) * mm, "end": v(17.49, 9.75) * mm});
            skLineSegment(sketch, "E78.2.50", {"start": v(18.8, 14.62) * mm, "end": v(18.76, 14.54) * mm});
            skLineSegment(sketch, "E78.2.51", {"start": v(19.28, 13.61) * mm, "end": v(19.18, 13.87) * mm});
            skLineSegment(sketch, "E78.2.52", {"start": v(18.6, 14.25) * mm, "end": v(18.5, 14.06) * mm});
            skLineSegment(sketch, "E78.2.53", {"start": v(19.07, 14.14) * mm, "end": v(18.99, 14.34) * mm});
            skLineSegment(sketch, "E78.2.54", {"start": v(18.84, 14.66) * mm, "end": v(18.83, 14.66) * mm});
            skLineSegment(sketch, "E78.2.55", {"start": v(18.5, 14.06) * mm, "end": v(18.39, 13.87) * mm});
            skLineSegment(sketch, "E78.2.56", {"start": v(19.18, 13.87) * mm, "end": v(19.07, 14.14) * mm});
            skLineSegment(sketch, "E78.2.57", {"start": v(18.69, 14.4) * mm, "end": v(18.6, 14.25) * mm});
            skLineSegment(sketch, "E78.2.58", {"start": v(18.86, 14.63) * mm, "end": v(18.84, 14.66) * mm});
            skLineSegment(sketch, "E78.2.59", {"start": v(19.31, 13.52) * mm, "end": v(19.28, 13.61) * mm});
            skLineSegment(sketch, "E78.2.60", {"start": v(18.88, 14.58) * mm, "end": v(18.86, 14.63) * mm});
            skLineSegment(sketch, "E78.2.61", {"start": v(18.93, 14.49) * mm, "end": v(18.88, 14.58) * mm});
            skLineSegment(sketch, "E78.2.62", {"start": v(18.99, 14.34) * mm, "end": v(18.93, 14.49) * mm});
            skLineSegment(sketch, "E78.2.63", {"start": v(18.83, 14.65) * mm, "end": v(18.8, 14.62) * mm});
            skLineSegment(sketch, "E78.2.64", {"start": v(18.83, 14.66) * mm, "end": v(18.83, 14.65) * mm});
            skLineSegment(sketch, "E78.2.65", {"start": v(18.83, 14.66) * mm, "end": v(18.83, 14.66) * mm});
            skLineSegment(sketch, "E78.2.66", {"start": v(18.76, 14.54) * mm, "end": v(18.69, 14.4) * mm});
            skSolve(sketch);
        }
        {
            var Q0;
            Q0=makeQuery(id+"F3.imprint","IMPRINT",FACE,{"disambiguationData":[TD([[makeQuery(id+"F3.imprint","IMPRINT",EDGE,{"derivedFrom":sQuery(id+"F3.wireOp",EDGE,"E78.1.0")}),1.0]])]});
            var Q1;
            Q1=makeQuery(id+"F3.imprint","IMPRINT",FACE,{"disambiguationData":[TD([[makeQuery(id+"F3.imprint","IMPRINT",EDGE,{"derivedFrom":sQuery(id+"F3.wireOp",EDGE,"E78.2.0")}),1.0]])]});
            var Q2;
            Q2=makeQuery(id+"F3.imprint","IMPRINT",FACE,{"disambiguationData":[TD([[makeQuery(id+"F3.imprint","IMPRINT",EDGE,{"derivedFrom":sQuery(id+"F3.wireOp",EDGE,"E10")}),1.0]])]});
            extrude(context, id + "F4", {"entities" : qUnion([Q0, Q1, Q2]), "operationType" : NewBodyOperationType.REMOVE, "oppositeDirection" : true, "depth" : 25.4 * mm, "offsetDistance" : 25.4 * mm});
        }
    });
